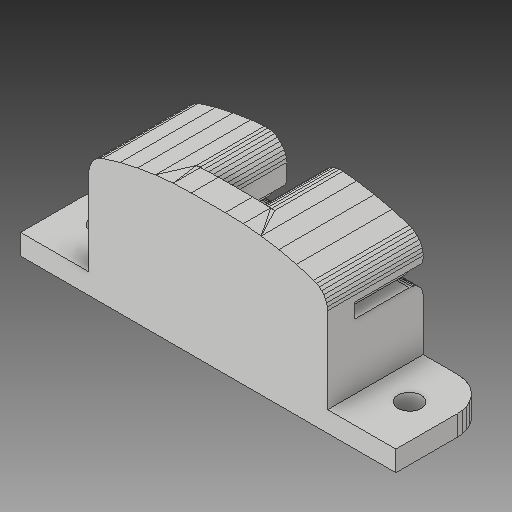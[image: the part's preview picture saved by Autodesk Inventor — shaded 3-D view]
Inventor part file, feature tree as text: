
AUTODESK INVENTOR PART (.ipt)
format: ipt  version: 2017 (Build 210142000, 142)  size: 396,288 bytes
history: native  units: mm
features: other x3, sketch x1
ambient origin geometry x8: Origin, YZ Plane, XZ Plane, XY Plane, X Axis, Y Axis, Z Axis, Center Point
bodies: Solid1 (feature_tree)
feature tree (4):
  other  "Y Belt Clamp.ipt"
  other  "Solid1::Y Belt Clamp.ipt"
  other  "TaggingFeature1"
  sketch  "Sketch2"  dims[d0=10.0mm]
